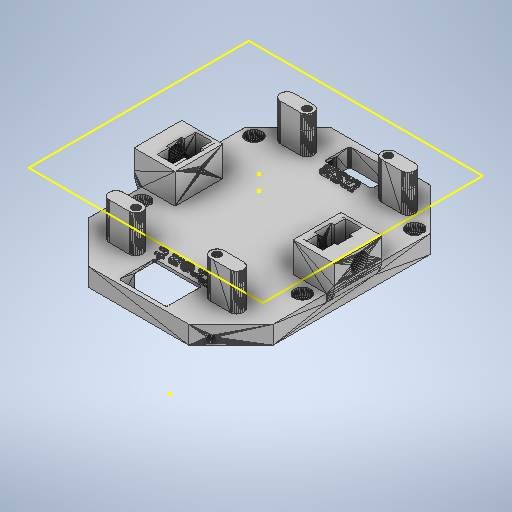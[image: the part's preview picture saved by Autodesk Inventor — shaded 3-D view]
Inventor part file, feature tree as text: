
AUTODESK INVENTOR PART (.ipt)
format: ipt  version: 2025.3 (Build 293356030, 356C)  size: 4,988,416 bytes
history: native  units: mm
features: other x3, sketch x1
ambient origin geometry x8: Origin, YZ Plane, XZ Plane, XY Plane, X Axis, Y Axis, Z Axis, Center Point
bodies: Solid1 (feature_tree)
feature tree (4):
  other  "chasis_b v1.ipt"
  other  "Solid1::chasis_b v1.ipt"
  other  "OperaciónIdentificador1"
  sketch  "Boceto1"  dims[d0=1.0mm d1=1.0mm]
